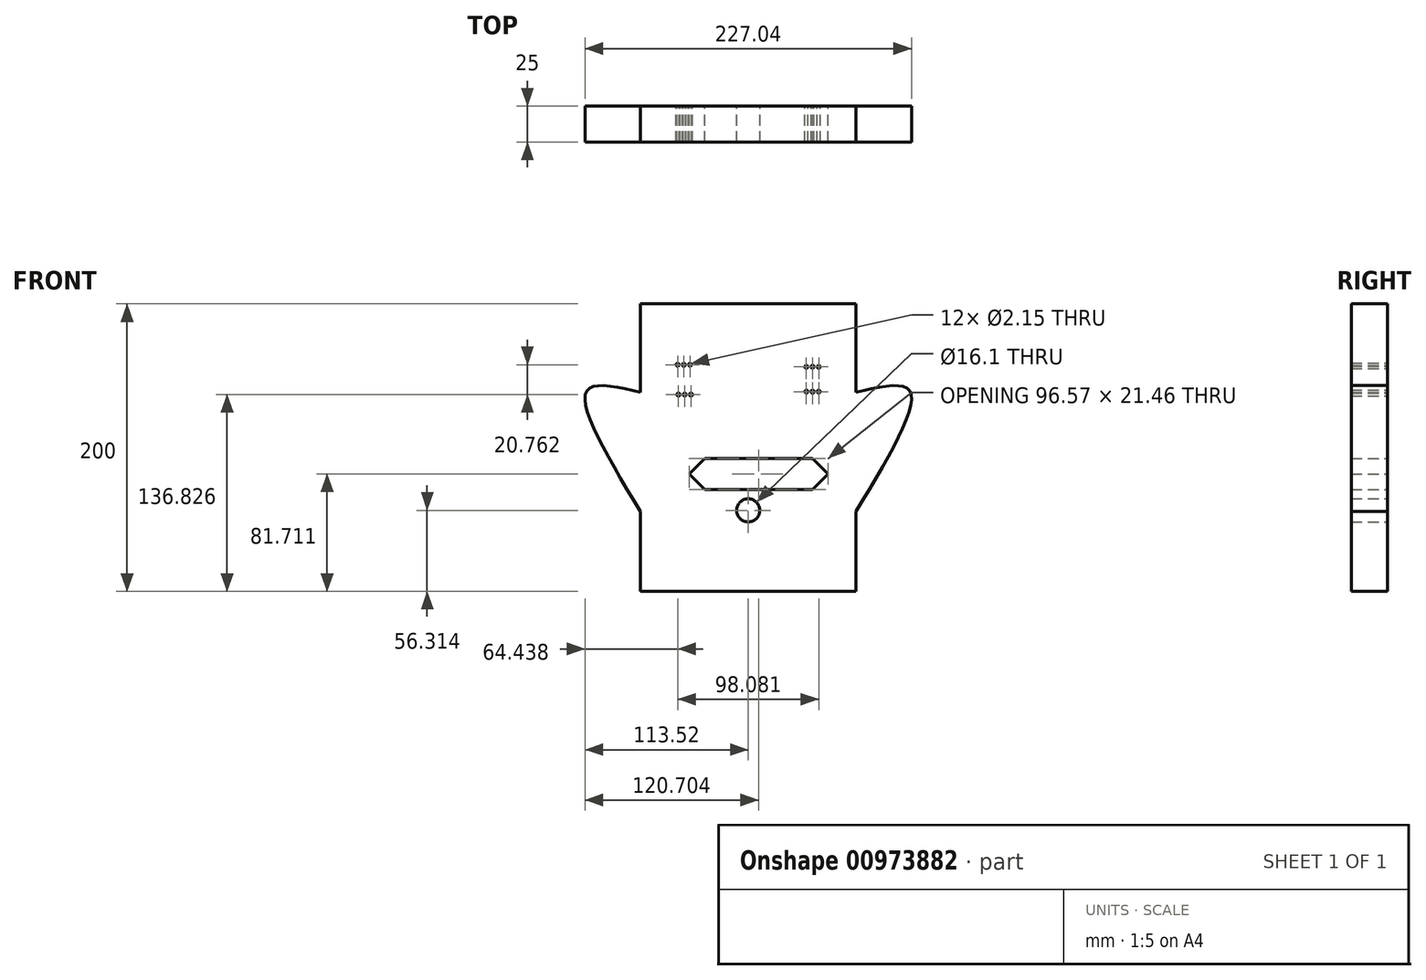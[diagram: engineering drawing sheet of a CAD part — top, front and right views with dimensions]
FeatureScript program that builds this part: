
annotation { "Feature Type Name" : "Feature", "Feature Type Description" : "" }
export const myFeature = defineFeature(function(context is Context, id is Id, definition is map)
    precondition{}
    {
        {
            var Q0;
            Q0=qCreatedBy(makeId("Front.planeOp"),FACE);
            var sketch = newSketch(context, id + "F0", { "sketchPlane" : qUnion([Q0])});
            skLineSegment(sketch, "E0.top", {"start": v(-30.37, -21.29) * mm, "end": v(44.74, -21.29) * mm});
            skLineSegment(sketch, "E1", {"start": v(-41.1, -10.56) * mm, "end": v(-30.37, -21.29) * mm});
            skLineSegment(sketch, "E2", {"start": v(44.74, 0.17) * mm, "end": v(55.47, -10.56) * mm});
            skLineSegment(sketch, "E3", {"start": v(55.47, -10.56) * mm, "end": v(44.74, -21.29) * mm});
            skLineSegment(sketch, "E4", {"start": v(-30.37, 0.17) * mm, "end": v(-41.1, -10.56) * mm});
            skLineSegment(sketch, "E5", {"start": v(-30.37, 0.17) * mm, "end": v(-30.37, -21.29) * mm});
            skLineSegment(sketch, "E6", {"start": v(44.74, 0.17) * mm, "end": v(44.74, -21.29) * mm});
            skCircle(sketch, "E7", {"center": v(-49.08, 65.32) * mm, "radius": 1.07 * mm});
            skCircle(sketch, "E8.0.1.0", {"center": v(-48.48, 44.56) * mm, "radius": 1.07 * mm});
            skCircle(sketch, "E8.1.0.0", {"center": v(-44.79, 65.32) * mm, "radius": 1.07 * mm});
            skCircle(sketch, "E8.1.1.0", {"center": v(-44.18, 44.56) * mm, "radius": 1.07 * mm});
            skCircle(sketch, "E8.2.0.0", {"center": v(-40.49, 65.32) * mm, "radius": 1.07 * mm});
            skCircle(sketch, "E8.2.1.0", {"center": v(-39.89, 44.56) * mm, "radius": 1.07 * mm});
            skCircle(sketch, "E9", {"center": v(49, 63.9) * mm, "radius": 1.07 * mm});
            skCircle(sketch, "E10.0.1.0", {"center": v(49, 46.63) * mm, "radius": 1.07 * mm});
            skCircle(sketch, "E10.1.0.0", {"center": v(44.7, 63.9) * mm, "radius": 1.07 * mm});
            skCircle(sketch, "E10.1.1.0", {"center": v(44.7, 46.63) * mm, "radius": 1.07 * mm});
            skCircle(sketch, "E10.2.0.0", {"center": v(40.4, 63.9) * mm, "radius": 1.07 * mm});
            skCircle(sketch, "E10.2.1.0", {"center": v(40.4, 46.63) * mm, "radius": 1.07 * mm});
            skLineSegment(sketch, "E10.direction1", {"start": v(49, 63.9) * mm, "end": v(44.7, 63.9) * mm, "construction": true});
            skCircle(sketch, "E11", {"center": v(0, -35.96) * mm, "radius": 8.05 * mm});
            skLineSegment(sketch, "E12.bottom", {"start": v(75, 107.73) * mm, "end": v(-75, 107.73) * mm});
            skLineSegment(sketch, "E12.top", {"start": v(75, -92.27) * mm, "end": v(-75, -92.27) * mm});
            skLineSegment(sketch, "E12.left", {"start": v(75, 107.73) * mm, "end": v(75, -92.27) * mm});
            skLineSegment(sketch, "E12.right", {"start": v(-75, 107.73) * mm, "end": v(-75, -92.27) * mm});
            skLineSegment(sketch, "E13", {"start": v(-30.37, 0.17) * mm, "end": v(44.74, 0.17) * mm});
            skFitSpline(sketch, "E14", {"points": [v(75, 46.03) * mm, v(112.17, 47.25) * mm, v(75, -36.69) * mm], "startDerivative": vector(126, 30.46) * mm, "endDerivative": vector(-108.62, -180.3) * mm});
            skFitSpline(sketch, "E15.MirrorCS", {"points": [v(-75, 46.03) * mm, v(-112.17, 47.25) * mm, v(-75, -36.69) * mm], "startDerivative": vector(-126, 30.46) * mm, "endDerivative": vector(108.62, -180.3) * mm});
            skSolve(sketch);
        }
        {
            var Q0;
            Q0 = qSketchRegion(id + "F0", true);
            extrude(context, id + "F1", {"entities" : qUnion([Q0]), "depth" : 25 * mm, "offsetDistance" : 25 * mm});
        }
        {
            var Q0;
            Q0=sQuery(id+"F0.wireOp",EDGE,"E5");
            var Q1;
            Q1=sQuery(id+"F0.wireOp",EDGE,"E6");
            extrude(context, id + "F2", {"bodyType" : ToolBodyType.SURFACE, "surfaceEntities" : qUnion([Q0, Q1]), "depth" : 25 * mm, "offsetDistance" : 25 * mm});
        }
    });
